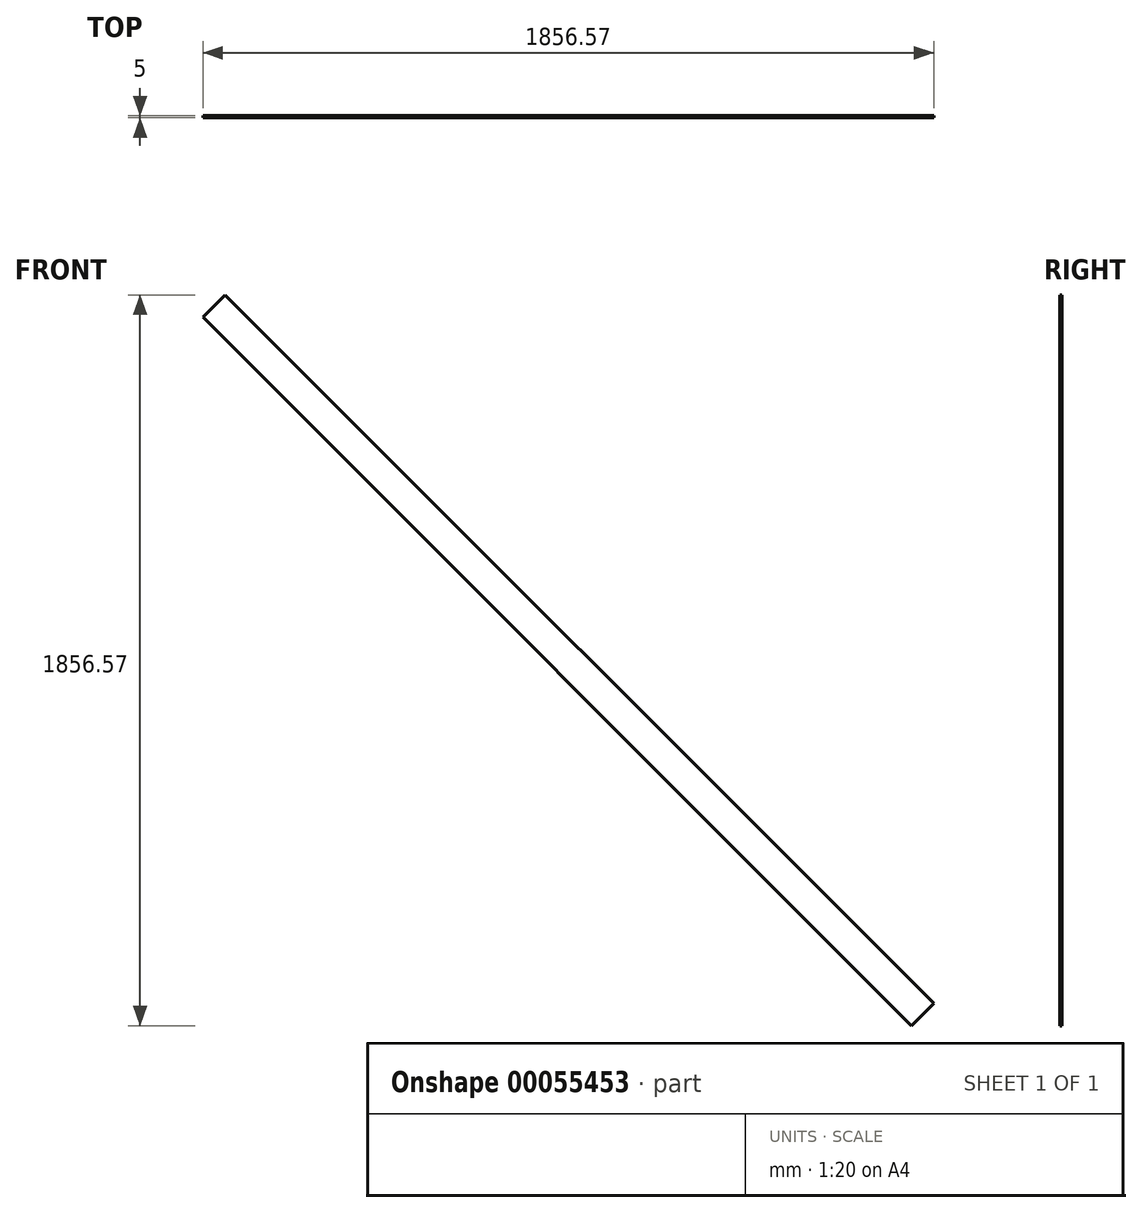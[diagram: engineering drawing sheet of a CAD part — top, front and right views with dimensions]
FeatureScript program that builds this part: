
annotation { "Feature Type Name" : "Feature", "Feature Type Description" : "" }
export const myFeature = defineFeature(function(context is Context, id is Id, definition is map)
    precondition{}
    {
        {
            var Q0;
            Q0=qCreatedBy(makeId("Front.planeOp"),FACE);
            var sketch = newSketch(context, id + "F0", { "sketchPlane" : qUnion([Q0])});
            skLineSegment(sketch, "E0", {"start": v(1800, 0) * mm, "end": v(0, 1800) * mm});
            skLineSegment(sketch, "E1", {"start": v(0, 1800) * mm, "end": v(56.57, 1856.57) * mm});
            skLineSegment(sketch, "E2", {"start": v(1800, 0) * mm, "end": v(1856.57, 56.57) * mm});
            skLineSegment(sketch, "E3", {"start": v(1856.57, 56.57) * mm, "end": v(56.57, 1856.57) * mm});
            skSolve(sketch);
        }
        {
            var Q0;
            Q0 = qSketchRegion(id + "F0", true);
            extrude(context, id + "F1", {"entities" : qUnion([Q0]), "oppositeDirection" : true, "depth" : 5 * mm});
        }
    });
